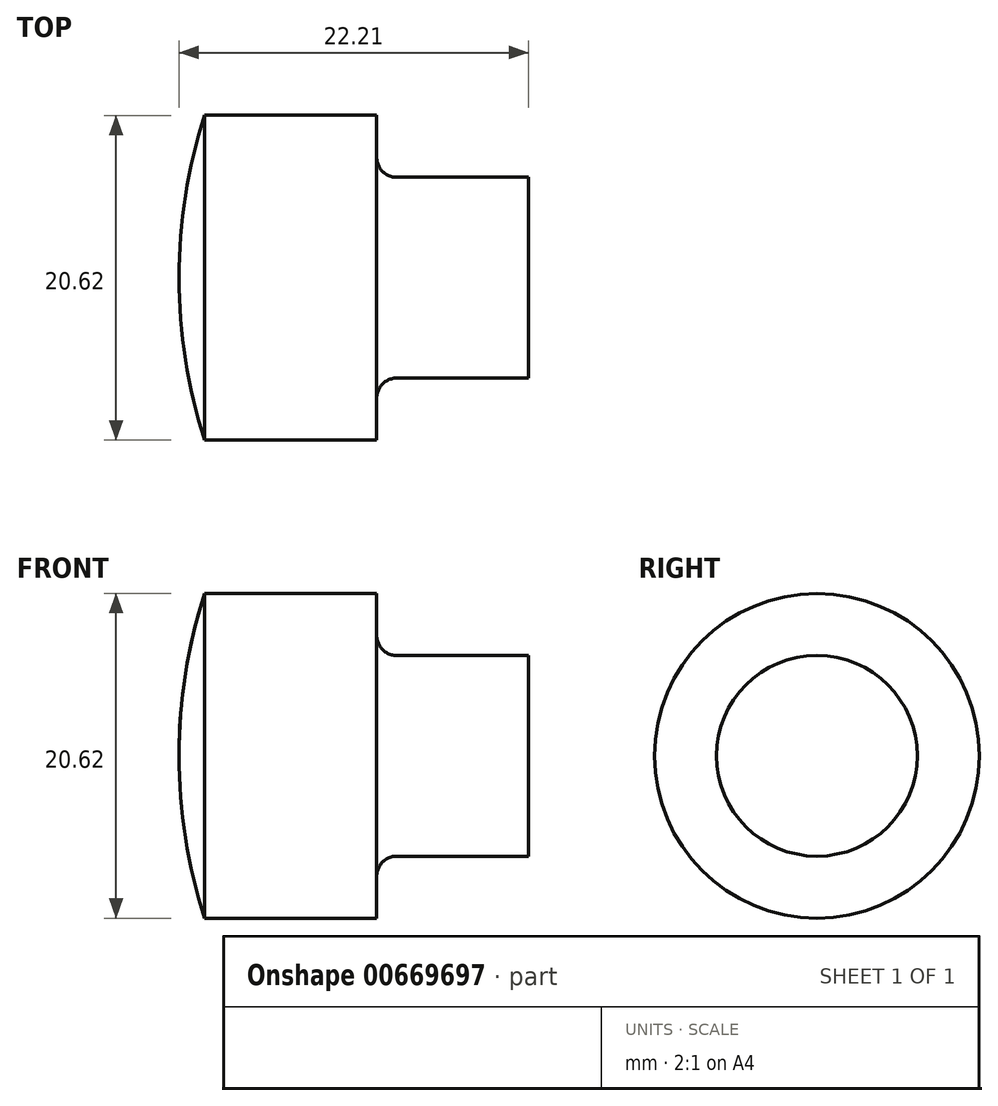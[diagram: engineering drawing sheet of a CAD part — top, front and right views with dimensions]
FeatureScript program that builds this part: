
annotation { "Feature Type Name" : "Feature", "Feature Type Description" : "" }
export const myFeature = defineFeature(function(context is Context, id is Id, definition is map)
    precondition{}
    {
        {
            var Q0;
            Q0=qCreatedBy(makeId("Front.planeOp"),FACE);
            var sketch = newSketch(context, id + "F0", { "sketchPlane" : qUnion([Q0])});
            skLineSegment(sketch, "E0", {"start": v(11.18, 0) * mm, "end": v(-24.9, 0) * mm, "construction": true});
            skLineSegment(sketch, "E1.bottom", {"start": v(0, 0) * mm, "end": v(-22.2, 0) * mm});
            skLineSegment(sketch, "E1.top", {"start": v(-9.65, 10.31) * mm, "end": v(-20.57, 10.31) * mm});
            skLineSegment(sketch, "E1.left", {"start": v(0, 0) * mm, "end": v(0, 6.38) * mm});
            skLineSegment(sketch, "E2", {"start": v(0, 6.38) * mm, "end": v(-8.38, 6.38) * mm});
            skLineSegment(sketch, "E3", {"start": v(-9.65, 7.65) * mm, "end": v(-9.65, 10.31) * mm});
            skPoint(sketch, "E4.visualSharp", {"position": v(-9.65, 6.38) * mm});
            skArc(sketch, "E4.filletArc", {"start": v(-9.65, 7.65) * mm, "mid": v(-9.28, 6.75) * mm, "end": v(-8.38, 6.38) * mm});
            skArc(sketch, "E5", {"start": v(-20.57, 10.31) * mm, "mid": v(-21.8, 5.22) * mm, "end": v(-22.2, 0) * mm});
            skSolve(sketch);
        }
        {
            var Q0;
            Q0=qSketchRegion(id+"F0",true);
            var Q1;
            Q1=sQuery(id+"F0.wireOp",EDGE,"E0");
            revolve(context, id + "F1", {"entities" : qUnion([Q0]), "axis" : qUnion([Q1]), "revolveType" : RevolveType.FULL});
        }
    });
